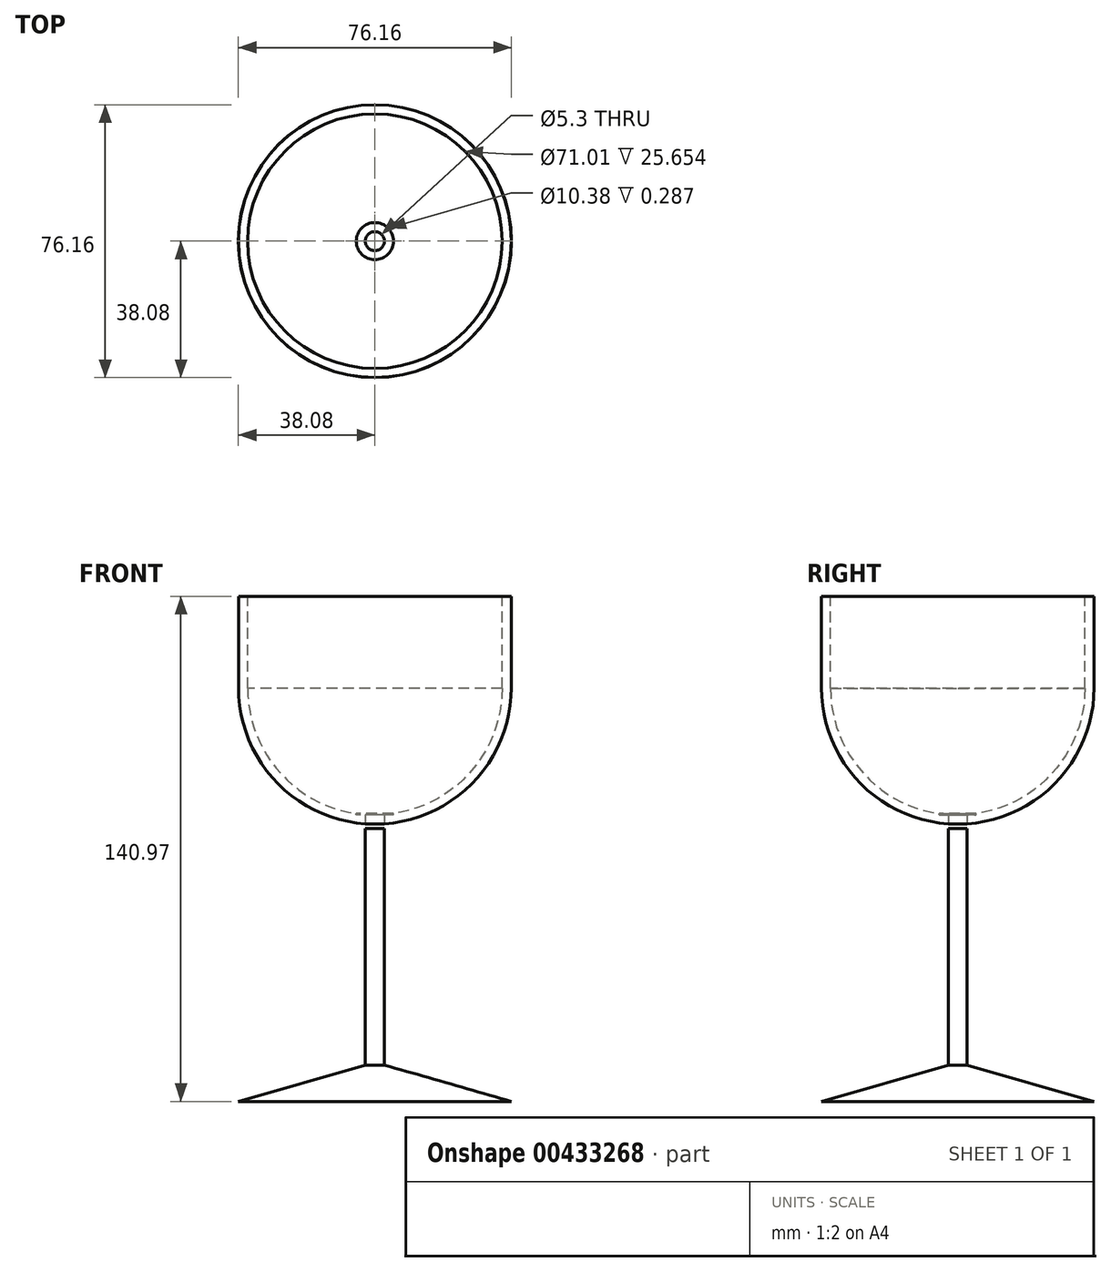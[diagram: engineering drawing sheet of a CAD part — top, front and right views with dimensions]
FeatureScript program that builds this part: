
annotation { "Feature Type Name" : "Feature", "Feature Type Description" : "" }
export const myFeature = defineFeature(function(context is Context, id is Id, definition is map)
    precondition{}
    {
        {
            var Q0;
            Q0=qCreatedBy(makeId("Top.planeOp"),FACE);
            var sketch = newSketch(context, id + "F0", { "sketchPlane" : qUnion([Q0])});
            skCircle(sketch, "E0", {"center": v(0, 0) * mm, "radius": 38.2 * mm});
            skSolve(sketch);
        }
        {
            var Q0;
            Q0=makeQuery(id+"F0.imprint","IMPRINT",FACE,{"disambiguationData":[TD([[makeQuery(id+"F0.imprint","IMPRINT",EDGE,{"derivedFrom":sQuery(id+"F0.wireOp",EDGE,"E0")}),1.0]])]});
            extrude(context, id + "F1", {"entities" : qUnion([Q0]), "depth" : 10.16 * mm});
        }
        {
            var Q0;
            Q0=makeQuery(id+"F1.opExtrude","CAP_EDGE",EDGE,{"disambiguationData":[OSD([sQuery(id+"F0.wireOp",EDGE,"E0")])],"isStart":false});
            chamfer(context, id + "F2", {"entities" : qUnion([Q0]), "chamferType" : ChamferType.OFFSET_ANGLE, "width" : 35.56 * mm, "oppositeDirection" : false, "angle" : 16 * degree, "tangentPropagation" : true});
        }
        {
            var Q0;
            Q0=makeQuery(id+"F1.opExtrude","CAP_FACE",FACE,{"disambiguationData":[OSD([sQuery(id+"F0.wireOp",EDGE,"E0")])],"isStart":false});
            var sketch = newSketch(context, id + "F3", { "sketchPlane" : qUnion([Q0])});
            skCircle(sketch, "E1", {"center": v(0, 0) * mm, "radius": 2.68 * mm});
            skSolve(sketch);
        }
        {
            var Q0;
            {var subQ0=sQuery(id+"F0.wireOp",EDGE,"E0");Q0=makeQuery(id+"F3.imprint","IMPRINT",FACE,{"disambiguationData":[TD([[makeQuery(id+"F3.imprint","IMPRINT",EDGE,{"derivedFrom":makeQuery(id+"F2.opChamfer","BLEND_EDGE",EDGE,{"blendedFrom":[makeQuery(id+"F1.opExtrude","CAP_EDGE",EDGE,{"disambiguationData":[OSD([subQ0])],"isStart":false}),makeQuery(id+"F1.opExtrude","CAP_FACE",FACE,{"disambiguationData":[OSD([subQ0])],"isStart":false})],"blendedInto":[makeQuery(id+"F1.opExtrude","CAP_FACE",FACE,{"disambiguationData":[OSD([subQ0])],"isStart":false})]})}),1.0]])]});}
            extrude(context, id + "F4", {"entities" : qUnion([Q0]), "operationType" : NewBodyOperationType.ADD, "depth" : 67.3 * mm});
        }
        {
            var Q0;
            Q0=makeQuery(id+"F4.opExtrude","CAP_FACE",FACE,{"disambiguationData":[OSD([sQuery(id+"F0.wireOp",EDGE,"E0")])],"isStart":false});
            var sketch = newSketch(context, id + "F5", { "sketchPlane" : qUnion([Q0])});
            skCircle(sketch, "E2", {"center": v(0, 0) * mm, "radius": 38.04 * mm});
            skSolve(sketch);
        }
        {
            var Q0;
            Q0=makeQuery(id+"F5.imprint","IMPRINT",FACE,{"disambiguationData":[TD([[makeQuery(id+"F5.imprint","IMPRINT",EDGE,{"derivedFrom":sQuery(id+"F5.wireOp",EDGE,"E2")}),1.0]])]});
            extrude(context, id + "F6", {"entities" : qUnion([Q0]), "depth" : 63.5 * mm});
        }
        {
            var Q0;
            Q0=makeQuery(id+"F4.opExtrude","CAP_FACE",FACE,{"disambiguationData":[OSD([sQuery(id+"F0.wireOp",EDGE,"E0")])],"isStart":false});
            extrude(context, id + "F7", {"entities" : qUnion([Q0]), "depth" : 63.5 * mm});
        }
        {
            var Q0;
            Q0=makeQuery(id+"F6.opExtrude","CAP_EDGE",EDGE,{"disambiguationData":[OSD([sQuery(id+"F5.wireOp",EDGE,"E2")])],"isStart":true});
            fillet(context, id + "F8", {"entities" : qUnion([Q0]), "radius" : 38.02 * mm, "tangentPropagation" : true, "allowEdgeOverflow" : false});
        }
        {
            var Q0;
            Q0=makeQuery(id+"F6.opExtrude","CAP_FACE",FACE,{"disambiguationData":[OSD([sQuery(id+"F0.wireOp",EDGE,"E0"),sQuery(id+"F5.wireOp",EDGE,"E2")])],"isStart":false});
            var sketch = newSketch(context, id + "F9", { "sketchPlane" : qUnion([Q0])});
            skCircle(sketch, "E3", {"center": v(0, 0) * mm, "radius": 35.5 * mm});
            skSolve(sketch);
        }
        {
            var Q0;
            Q0=makeQuery(id+"F9.imprint","IMPRINT",FACE,{"disambiguationData":[TD([[makeQuery(id+"F9.imprint","IMPRINT",EDGE,{"derivedFrom":sQuery(id+"F9.wireOp",EDGE,"E3")}),1.0]])]});
            extrude(context, id + "F10", {"entities" : qUnion([Q0]), "operationType" : NewBodyOperationType.REMOVE, "oppositeDirection" : true, "depth" : 25.65 * mm});
        }
        {
            var Q0;
            Q0=makeQuery(id+"F10.boolean.opBoolean","COPY",FACE,{"derivedFrom":makeQuery(id+"F10.opExtrude","CAP_FACE",FACE,{"disambiguationData":[OSD([sQuery(id+"F0.wireOp",EDGE,"E0"),sQuery(id+"F9.wireOp",EDGE,"E3")])],"isStart":false})});
            shell(context, id + "F11", {"entities" : qUnion([Q0]), "thickness" : 2.54 * mm});
        }
        {
            var Q0;
            Q0=makeQuery(id+"F7.opExtrude","CAP_FACE",FACE,{"disambiguationData":[OSD([sQuery(id+"F0.wireOp",EDGE,"E0")])],"isStart":false});
            extrude(context, id + "F12", {"entities" : qUnion([Q0]), "operationType" : NewBodyOperationType.REMOVE, "oppositeDirection" : true, "depth" : 64.77 * mm});
        }
        {
            var Q0;
            Q0=makeQuery(id+"F11.opShell","OFFSET_FACE",FACE,{"disambiguationData":[OSD([sQuery(id+"F0.wireOp",EDGE,"E0"),sQuery(id+"F9.wireOp",EDGE,"E3")])]});
            extrude(context, id + "F13", {"entities" : qUnion([Q0]), "operationType" : NewBodyOperationType.REMOVE, "oppositeDirection" : true, "depth" : 35.3 * mm});
        }
    });
